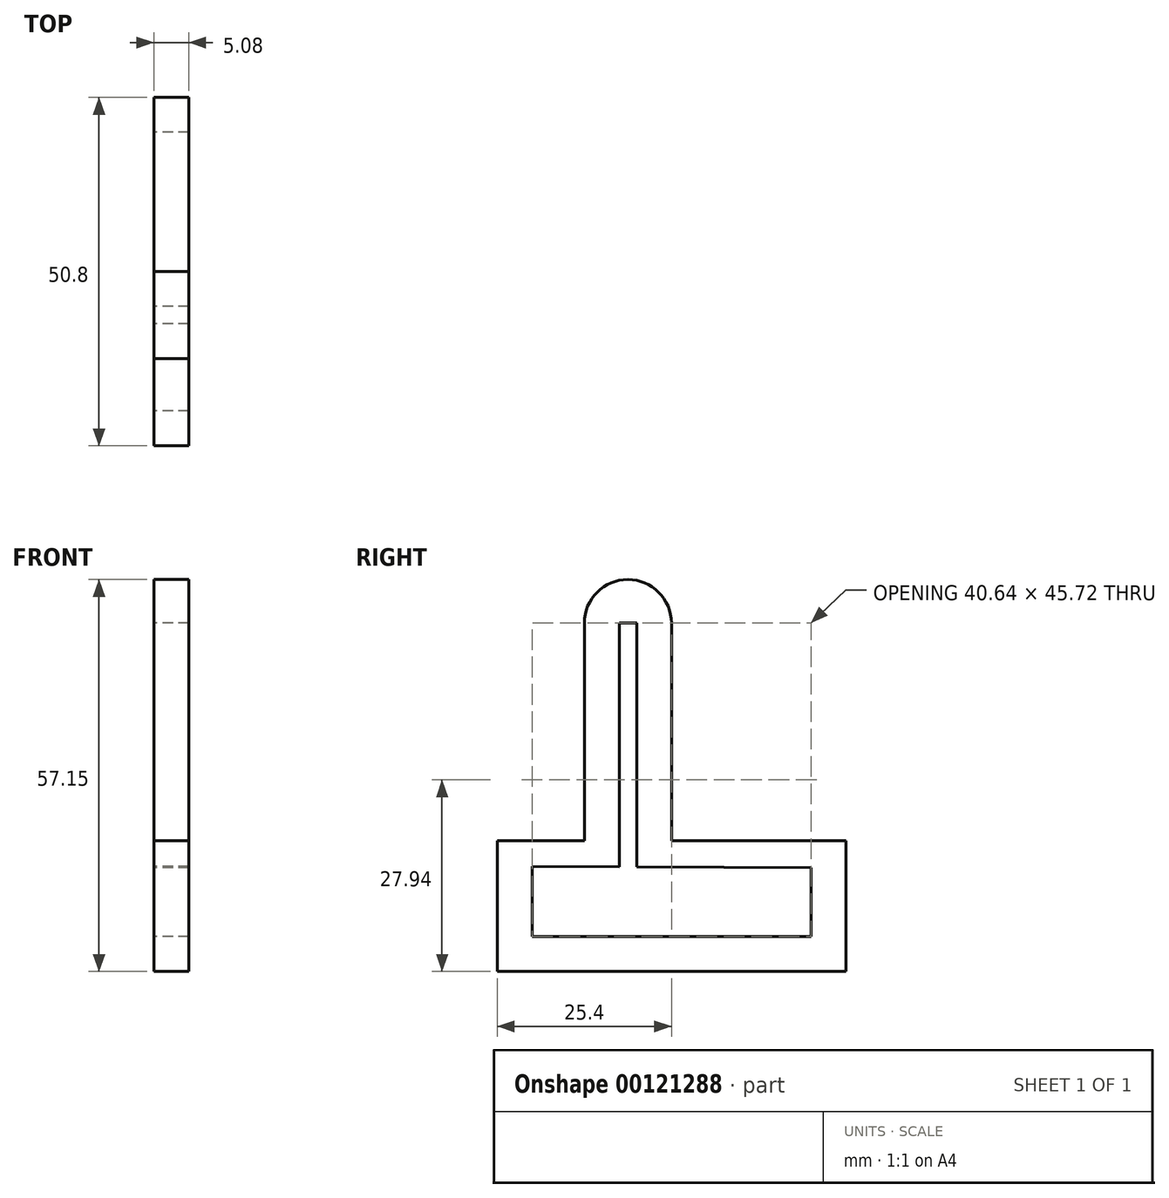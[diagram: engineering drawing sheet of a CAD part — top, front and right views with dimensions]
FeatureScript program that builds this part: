
annotation { "Feature Type Name" : "Feature", "Feature Type Description" : "" }
export const myFeature = defineFeature(function(context is Context, id is Id, definition is map)
    precondition{}
    {
        {
            var Q0;
            Q0=qCreatedBy(makeId("Right.planeOp"),FACE);
            var sketch = newSketch(context, id + "F0", { "sketchPlane" : qUnion([Q0])});
            skLineSegment(sketch, "E0", {"start": v(25.4, 0) * mm, "end": v(25.4, 19.05) * mm});
            skLineSegment(sketch, "E1", {"start": v(25.4, 19.05) * mm, "end": v(0, 19.05) * mm});
            skLineSegment(sketch, "E2", {"start": v(-25.4, 19.05) * mm, "end": v(-25.4, 0) * mm});
            skLineSegment(sketch, "E3", {"start": v(-25.4, 0) * mm, "end": v(25.4, 0) * mm});
            skLineSegment(sketch, "E4", {"start": v(-20.32, 15.3) * mm, "end": v(-20.32, 5.08) * mm});
            skLineSegment(sketch, "E5", {"start": v(-20.32, 5.08) * mm, "end": v(20.32, 5.08) * mm});
            skLineSegment(sketch, "E6", {"start": v(20.32, 5.08) * mm, "end": v(20.32, 15.15) * mm});
            skLineSegment(sketch, "E7", {"start": v(20.32, 15.15) * mm, "end": v(-5.08, 15.24) * mm});
            skLineSegment(sketch, "E8", {"start": v(-12.7, 19.05) * mm, "end": v(-12.7, 50.8) * mm});
            skLineSegment(sketch, "E9", {"start": v(-5.08, 19.05) * mm, "end": v(-5.08, 50.8) * mm});
            skLineSegment(sketch, "E10", {"start": v(-5.08, 50.8) * mm, "end": v(0, 50.8) * mm});
            skLineSegment(sketch, "E11", {"start": v(0, 50.8) * mm, "end": v(0, 19.05) * mm});
            skLineSegment(sketch, "E12", {"start": v(-12.7, 50.8) * mm, "end": v(-7.62, 50.8) * mm});
            skLineSegment(sketch, "E13", {"start": v(-7.62, 50.8) * mm, "end": v(-7.62, 19.05) * mm});
            skArc(sketch, "E14", {"start": v(0, 50.8) * mm, "mid": v(-6.35, 57.15) * mm, "end": v(-12.7, 50.8) * mm});
            skLineSegment(sketch, "E15", {"start": v(-7.62, 50.8) * mm, "end": v(-5.08, 50.8) * mm});
            skLineSegment(sketch, "E16", {"start": v(-7.62, 19.05) * mm, "end": v(-7.62, 15.25) * mm});
            skLineSegment(sketch, "E17", {"start": v(-5.08, 19.05) * mm, "end": v(-5.08, 15.24) * mm});
            skLineSegment(sketch, "E18.trimOffspring", {"start": v(-12.7, 19.05) * mm, "end": v(-25.4, 19.05) * mm});
            skLineSegment(sketch, "E19.trimOffspring", {"start": v(-7.62, 15.25) * mm, "end": v(-20.32, 15.3) * mm});
            skSolve(sketch);
        }
        {
            var Q0;
            Q0=makeQuery(id+"F0.imprint","IMPRINT",FACE,{"disambiguationData":[TD([[makeQuery(id+"F0.imprint","IMPRINT",EDGE,{"derivedFrom":sQuery(id+"F0.wireOp",EDGE,"E0")}),1.0]])]});
            var Q1;
            {var subQ0=sQuery(id+"F0.wireOp",EDGE,"E8");Q1=makeQuery(id+"F0.imprint","IMPRINT",FACE,{"disambiguationData":[TD([[makeQuery(id+"F0.imprint","IMPRINT",EDGE,{"derivedFrom":subQ0}),-1.0]])]});}
            var Q2;
            {var subQ0=sQuery(id+"F0.wireOp",EDGE,"E9");Q2=makeQuery(id+"F0.imprint","IMPRINT",FACE,{"disambiguationData":[TD([[makeQuery(id+"F0.imprint","IMPRINT",EDGE,{"derivedFrom":subQ0}),-1.0]])]});}
            var Q3;
            Q3=makeQuery(id+"F0.imprint","IMPRINT",FACE,{"disambiguationData":[TD([[makeQuery(id+"F0.imprint","IMPRINT",EDGE,{"derivedFrom":sQuery(id+"F0.wireOp",EDGE,"E10")}),1.0]])]});
            extrude(context, id + "F1", {"entities" : qUnion([Q0, Q1, Q2, Q3]), "depth" : 5.08 * mm});
        }
    });
